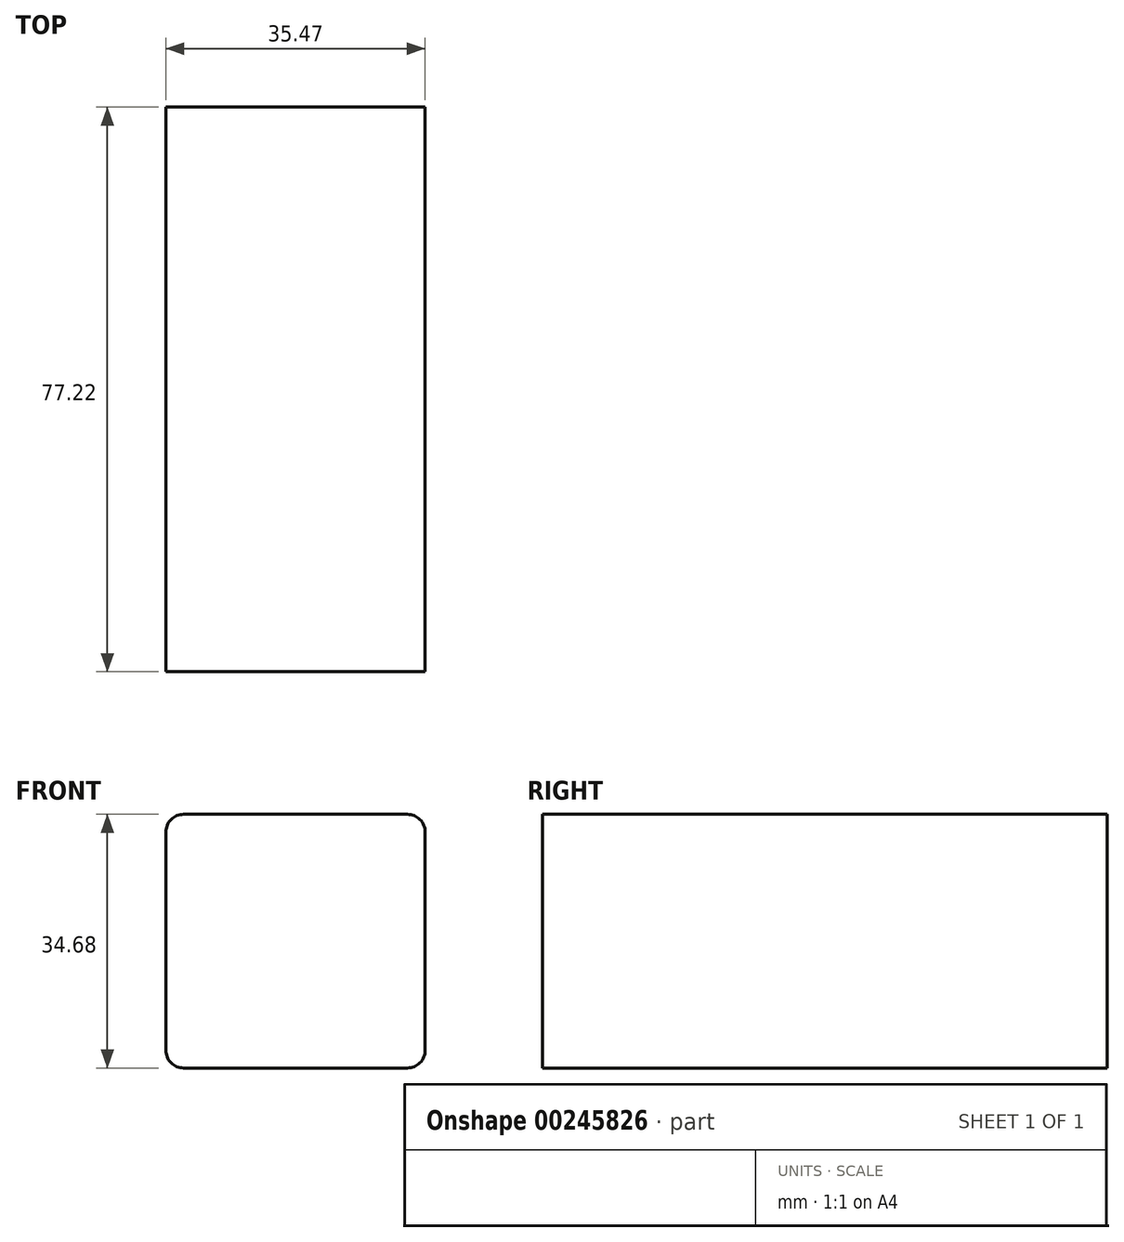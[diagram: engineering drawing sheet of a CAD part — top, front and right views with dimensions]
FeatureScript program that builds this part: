
annotation { "Feature Type Name" : "Feature", "Feature Type Description" : "" }
export const myFeature = defineFeature(function(context is Context, id is Id, definition is map)
    precondition{}
    {
        {
            var Q0;
            Q0=qCreatedBy(makeId("Front.planeOp"),FACE);
            var sketch = newSketch(context, id + "F0", { "sketchPlane" : qUnion([Q0])});
            skLineSegment(sketch, "E0.bottom", {"start": v(-21.87, 24.83) * mm, "end": v(13.6, 24.83) * mm});
            skLineSegment(sketch, "E0.top", {"start": v(-21.87, -9.85) * mm, "end": v(13.6, -9.85) * mm});
            skLineSegment(sketch, "E0.left", {"start": v(-21.87, 24.83) * mm, "end": v(-21.87, -9.85) * mm});
            skLineSegment(sketch, "E0.right", {"start": v(13.6, 24.83) * mm, "end": v(13.6, -9.85) * mm});
            skSolve(sketch);
        }
        {
            var Q0;
            Q0=makeQuery(id+"F0.imprint","IMPRINT",FACE,{"disambiguationData":[TD([[makeQuery(id+"F0.imprint","IMPRINT",EDGE,{"derivedFrom":sQuery(id+"F0.wireOp",EDGE,"E0.bottom")}),-1.0]])]});
            extrude(context, id + "F1", {"entities" : qUnion([Q0]), "depth" : 77.22 * mm});
        }
        {
            var Q0;
            Q0=makeQuery(id+"F1.opExtrude","SWEPT_EDGE",EDGE,{"disambiguationData":[OSD([sQuery(id+"F0.wireOp",EDGE,"E0.bottom"),sQuery(id+"F0.wireOp",EDGE,"E0.right")])]});
            var Q1;
            Q1=makeQuery(id+"F1.opExtrude","SWEPT_EDGE",EDGE,{"disambiguationData":[OSD([sQuery(id+"F0.wireOp",EDGE,"E0.bottom"),sQuery(id+"F0.wireOp",EDGE,"E0.left")])]});
            var Q2;
            Q2=makeQuery(id+"F1.opExtrude","SWEPT_EDGE",EDGE,{"disambiguationData":[OSD([sQuery(id+"F0.wireOp",EDGE,"E0.top"),sQuery(id+"F0.wireOp",EDGE,"E0.right")])]});
            fillet(context, id + "F2", {"entities" : qUnion([Q0, Q1, Q2]), "radius" : 2.45 * mm, "tangentPropagation" : true, "allowEdgeOverflow" : false});
        }
        {
            var Q0;
            Q0=makeQuery(id+"F1.opExtrude","SWEPT_EDGE",EDGE,{"disambiguationData":[OSD([sQuery(id+"F0.wireOp",EDGE,"E0.top"),sQuery(id+"F0.wireOp",EDGE,"E0.left")])]});
            fillet(context, id + "F3", {"entities" : qUnion([Q0]), "radius" : 2.45 * mm, "tangentPropagation" : true, "allowEdgeOverflow" : false});
        }
    });
